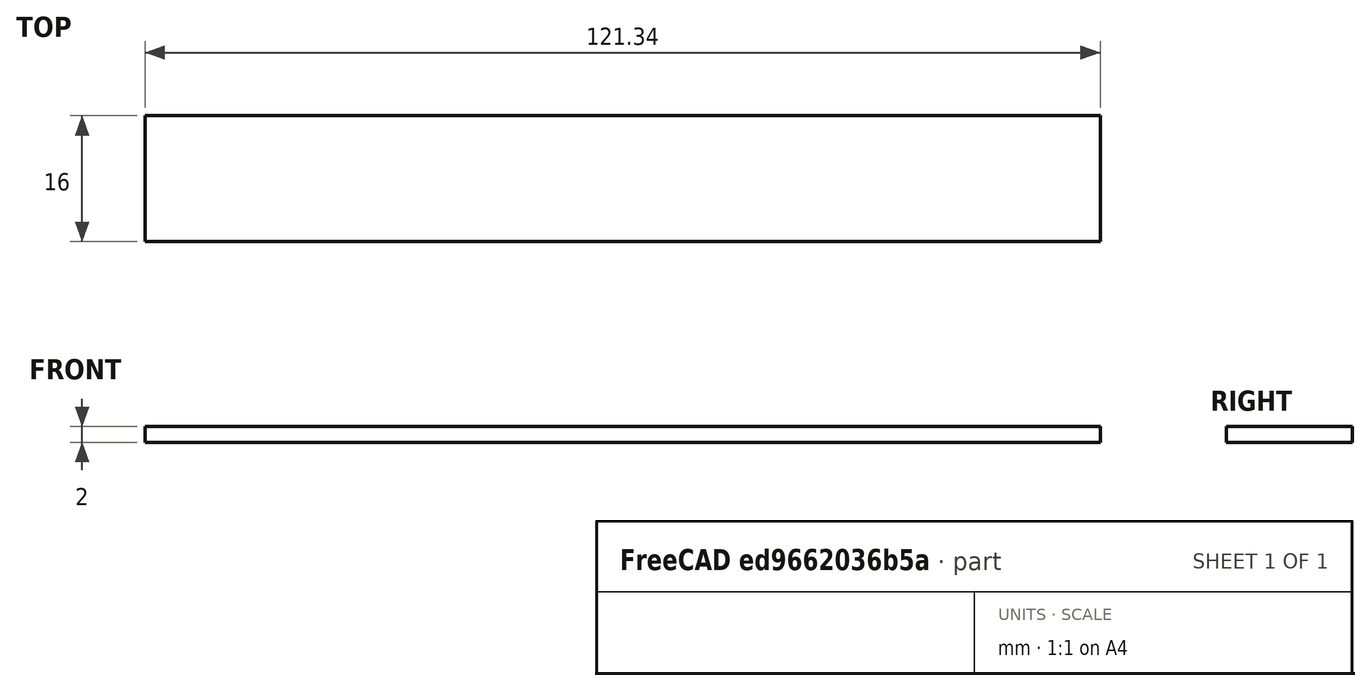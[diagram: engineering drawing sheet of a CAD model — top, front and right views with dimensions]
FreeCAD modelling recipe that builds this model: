
FCSTD DOCUMENT  (FreeCAD 0.18.4R)
Label: 17
License: All rights reserved
LicenseURL: http://en.wikipedia.org/wiki/All_rights_reserved
objects: Mesh::Feature×2, Sketcher::SketchObject×1, PartDesign::Pad×1, PartDesign::Body×1
note: 4 computed .brp shape members not serialized (recipe doc carries the construction recipe); baked Part::Feature solids carry a one-line shape summary decoded from their .brp

FEATURE [Mesh::Feature] bore_holder_Body  label="bore_holder-Body"
FEATURE [Sketcher::SketchObject] Sketch  label="Unnamed"
  constraints (10):
    c: Coincident(g0,g1)
    c: Coincident(g1,g2)
    c: Coincident(g2,g3)
    c: Coincident(g3,g0)
    c: Horizontal(g0)
    c: Horizontal(g2)
    c: Vertical(g1)
    c: Vertical(g3)
    c: PointOnObject(g0,g-1)
    c: Distance(g1) = 2
FEATURE [PartDesign::Pad] Pad  label="Unnamed"
  Length = 100
  Length2 = 100
  Type = 0
FEATURE [PartDesign::Body] Body
  Group = -> [Sketch,Pad]
  Origin = -> Origin
  Tip = -> Pad
FEATURE [Mesh::Feature] ____________4  label="Unnamed"
